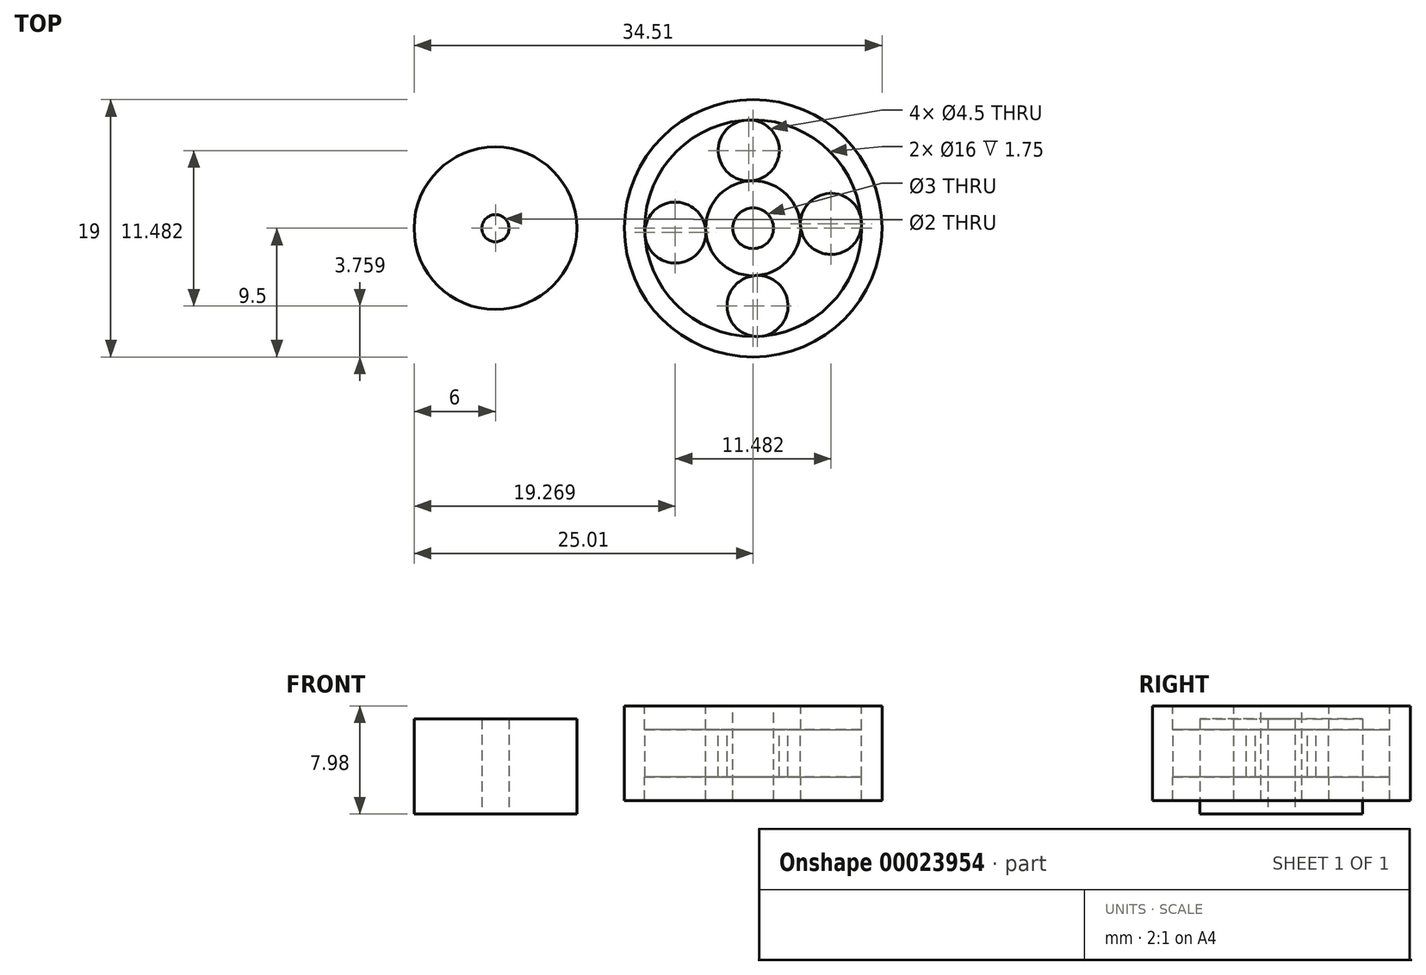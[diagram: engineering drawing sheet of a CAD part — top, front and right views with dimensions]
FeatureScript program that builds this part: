
annotation { "Feature Type Name" : "Feature", "Feature Type Description" : "" }
export const myFeature = defineFeature(function(context is Context, id is Id, definition is map)
    precondition{}
    {
        {
            var Q0;
            Q0=qCreatedBy(makeId("Front.planeOp"),FACE);
            var sketch = newSketch(context, id + "F0", { "sketchPlane" : qUnion([Q0])});
            skLineSegment(sketch, "E0", {"start": v(0, 0) * mm, "end": v(0, 5.03) * mm, "construction": true});
            skLineSegment(sketch, "E1", {"start": v(1, 0) * mm, "end": v(1, 7) * mm});
            skLineSegment(sketch, "E2.bottom", {"start": v(1, 7) * mm, "end": v(6, 7) * mm});
            skLineSegment(sketch, "E2.top", {"start": v(1, 0) * mm, "end": v(6, 0) * mm});
            skLineSegment(sketch, "E2.left", {"start": v(1, 7) * mm, "end": v(1, 0) * mm});
            skLineSegment(sketch, "E2.right", {"start": v(6, 7) * mm, "end": v(6, 0) * mm});
            skSolve(sketch);
        }
        {
            var Q0;
            Q0 = qSketchRegion(id + "F0", true);
            var Q1;
            Q1=sQuery(id+"F0.wireOp",EDGE,"E0");
            revolve(context, id + "F1", {"entities" : qUnion([Q0]), "axis" : qUnion([Q1]), "revolveType" : RevolveType.FULL});
        }
        {
            var Q0;
            Q0=qCreatedBy(makeId("Front.planeOp"),FACE);
            var sketch = newSketch(context, id + "F2", { "sketchPlane" : qUnion([Q0])});
            skLineSegment(sketch, "E3", {"start": v(20.5, 0.98) * mm, "end": v(20.5, 7.98) * mm});
            skLineSegment(sketch, "E4.bottom", {"start": v(20.5, 7.98) * mm, "end": v(22.5, 7.98) * mm});
            skLineSegment(sketch, "E4.top", {"start": v(20.5, 0.98) * mm, "end": v(22.5, 0.98) * mm});
            skLineSegment(sketch, "E4.left", {"start": v(20.5, 7.98) * mm, "end": v(20.5, 0.98) * mm});
            skLineSegment(sketch, "E4.right", {"start": v(22.5, 7.98) * mm, "end": v(22.5, 0.98) * mm});
            skLineSegment(sketch, "E5.bottom", {"start": v(22.5, 6.23) * mm, "end": v(27, 6.23) * mm});
            skLineSegment(sketch, "E5.top", {"start": v(22.5, 2.73) * mm, "end": v(27, 2.73) * mm});
            skLineSegment(sketch, "E5.left", {"start": v(22.5, 6.23) * mm, "end": v(22.5, 2.73) * mm});
            skLineSegment(sketch, "E5.right", {"start": v(27, 6.23) * mm, "end": v(27, 2.73) * mm});
            skLineSegment(sketch, "E6.bottom", {"start": v(27, 7.98) * mm, "end": v(28.5, 7.98) * mm});
            skLineSegment(sketch, "E6.top", {"start": v(27, 0.98) * mm, "end": v(28.5, 0.98) * mm});
            skLineSegment(sketch, "E6.left", {"start": v(27, 7.98) * mm, "end": v(27, 0.98) * mm});
            skLineSegment(sketch, "E6.right", {"start": v(28.5, 7.98) * mm, "end": v(28.5, 0.98) * mm});
            skCircle(sketch, "E7", {"center": v(24.76, 6.23) * mm, "radius": 1.5 * mm, "construction": true});
            skLineSegment(sketch, "E8.trimOffspring", {"start": v(19, 0.98) * mm, "end": v(19, -21.9) * mm, "construction": true});
            skSolve(sketch);
        }
        {
            var Q0;
            Q0 = qSketchRegion(id + "F2", true);
            var Q1;
            Q1=sQuery(id+"F2.wireOp",EDGE,"E8.trimOffspring");
            revolve(context, id + "F3", {"entities" : qUnion([Q0]), "axis" : qUnion([Q1]), "revolveType" : RevolveType.FULL});
        }
        {
            var Q0;
            Q0=makeQuery(id+"F3.opRevolve","SWEPT_FACE",FACE,{"disambiguationData":[OSD([sQuery(id+"F2.wireOp",EDGE,"E5.bottom")])]});
            var sketch = newSketch(context, id + "F4", { "sketchPlane" : qUnion([Q0])});
            skCircle(sketch, "E9", {"center": v(18.69, 5.74) * mm, "radius": 2.25 * mm});
            skLineSegment(sketch, "E10", {"start": v(18.69, 5.74) * mm, "end": v(19, 0) * mm, "construction": true});
            skLineSegment(sketch, "E11", {"start": v(19, 0) * mm, "end": v(26.16, 0.4) * mm, "construction": true});
            skCircle(sketch, "E12", {"center": v(24.75, 0.32) * mm, "radius": 2.25 * mm});
            skLineSegment(sketch, "E13", {"start": v(19, 0) * mm, "end": v(19.4, -7.06) * mm, "construction": true});
            skCircle(sketch, "E14", {"center": v(19.33, -5.74) * mm, "radius": 2.25 * mm});
            skLineSegment(sketch, "E15", {"start": v(19, 0) * mm, "end": v(12.02, -0.4) * mm, "construction": true});
            skCircle(sketch, "E16", {"center": v(13.27, -0.32) * mm, "radius": 2.25 * mm});
            skSolve(sketch);
        }
        {
            var Q0;
            Q0 = qSketchRegion(id + "F4", true);
            extrude(context, id + "F5", {"entities" : qUnion([Q0]), "operationType" : NewBodyOperationType.REMOVE, "endBound" : BoundingType.THROUGH_ALL, "oppositeDirection" : true, "depth" : 25.4 * mm});
        }
    });
